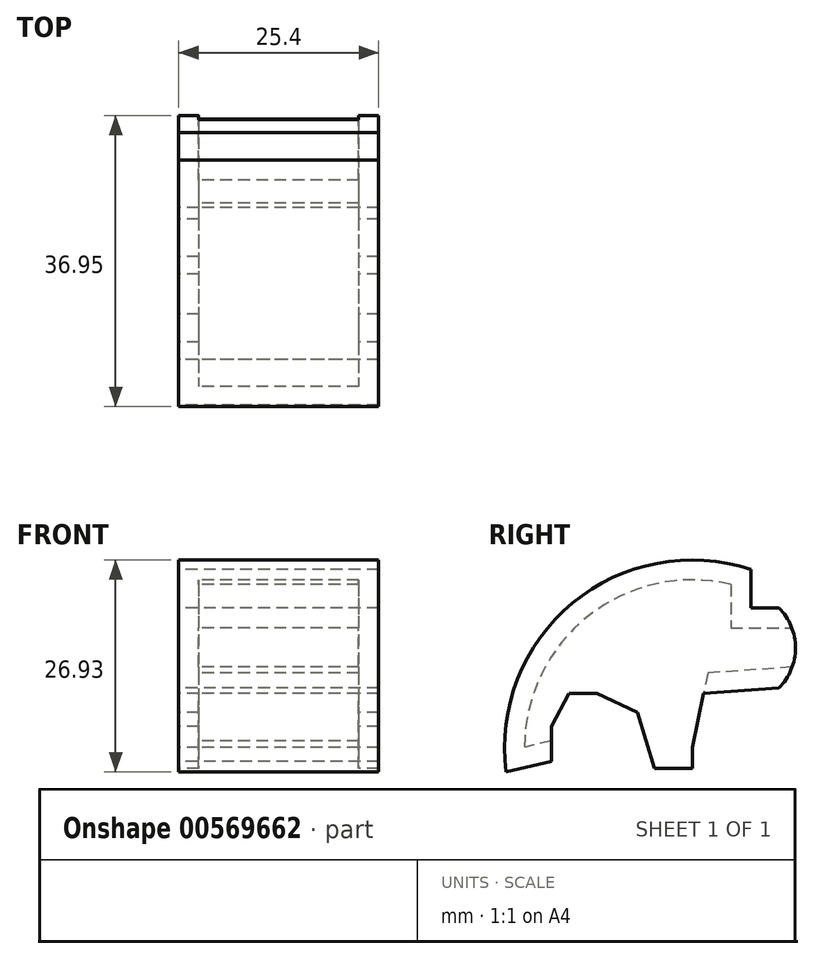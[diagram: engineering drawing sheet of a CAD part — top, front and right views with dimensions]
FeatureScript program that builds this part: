
annotation { "Feature Type Name" : "Feature", "Feature Type Description" : "" }
export const myFeature = defineFeature(function(context is Context, id is Id, definition is map)
    precondition{}
    {
        {
            var Q0;
            Q0=qCreatedBy(makeId("Right.planeOp"),FACE);
            var sketch = newSketch(context, id + "F0", { "sketchPlane" : qUnion([Q0])});
            skArc(sketch, "E0", {"start": v(39.95, 40) * mm, "mid": v(17.3, 35.7) * mm, "end": v(8.88, 14.25) * mm});
            skLineSegment(sketch, "E1", {"start": v(27.74, 14.7) * mm, "end": v(25.52, 21.8) * mm});
            skLineSegment(sketch, "E2", {"start": v(25.52, 21.8) * mm, "end": v(20.42, 24.24) * mm});
            skLineSegment(sketch, "E3", {"start": v(20.42, 24.24) * mm, "end": v(16.87, 24.24) * mm});
            skLineSegment(sketch, "E4", {"start": v(16.87, 24.24) * mm, "end": v(14.65, 20.02) * mm});
            skLineSegment(sketch, "E5", {"start": v(14.65, 20.02) * mm, "end": v(14.65, 15.58) * mm});
            skLineSegment(sketch, "E6", {"start": v(14.65, 15.58) * mm, "end": v(8.88, 14.25) * mm});
            skLineSegment(sketch, "E7", {"start": v(39.95, 40) * mm, "end": v(39.95, 35.1) * mm});
            skLineSegment(sketch, "E8", {"start": v(39.95, 35.1) * mm, "end": v(43.5, 35.1) * mm});
            skArc(sketch, "E9", {"start": v(43.5, 24.9) * mm, "mid": v(45.63, 30) * mm, "end": v(43.5, 35.1) * mm});
            skLineSegment(sketch, "E10", {"start": v(43.5, 24.9) * mm, "end": v(33.96, 24.24) * mm});
            skLineSegment(sketch, "E11", {"start": v(33.96, 24.24) * mm, "end": v(32.52, 17.34) * mm});
            skLineSegment(sketch, "E12", {"start": v(32.52, 14.7) * mm, "end": v(27.74, 14.7) * mm});
            skLineSegment(sketch, "E13", {"start": v(32.52, 17.34) * mm, "end": v(32.52, 14.7) * mm});
            skSolve(sketch);
        }
        {
            var Q0;
            Q0=makeQuery(id+"F0.imprint","IMPRINT",FACE,{"disambiguationData":[TD([[makeQuery(id+"F0.imprint","IMPRINT",EDGE,{"derivedFrom":sQuery(id+"F0.wireOp",EDGE,"E0")}),1.0]])]});
            extrude(context, id + "F1", {"entities" : qUnion([Q0]), "depth" : 25.4 * mm, "offsetDistance" : 25.4 * mm});
        }
        {
            var Q0;
            Q0=makeQuery(id+"F1.opExtrude","SWEPT_FACE",FACE,{"disambiguationData":[OSD([sQuery(id+"F0.wireOp",EDGE,"E5")])]});
            var Q1;
            Q1=makeQuery(id+"F1.opExtrude","SWEPT_FACE",FACE,{"disambiguationData":[OSD([sQuery(id+"F0.wireOp",EDGE,"E4")])]});
            var Q2;
            Q2=makeQuery(id+"F1.opExtrude","SWEPT_FACE",FACE,{"disambiguationData":[OSD([sQuery(id+"F0.wireOp",EDGE,"E11")])]});
            var Q3;
            Q3=makeQuery(id+"F1.opExtrude","SWEPT_FACE",FACE,{"disambiguationData":[OSD([sQuery(id+"F0.wireOp",EDGE,"E9")])]});
            var Q4;
            Q4=makeQuery(id+"F1.opExtrude","SWEPT_FACE",FACE,{"disambiguationData":[OSD([sQuery(id+"F0.wireOp",EDGE,"E12")])]});
            var Q5;
            Q5=makeQuery(id+"F1.opExtrude","SWEPT_FACE",FACE,{"disambiguationData":[OSD([sQuery(id+"F0.wireOp",EDGE,"E1")])]});
            var Q6;
            Q6=makeQuery(id+"F1.opExtrude","SWEPT_FACE",FACE,{"disambiguationData":[OSD([sQuery(id+"F0.wireOp",EDGE,"E2")])]});
            var Q7;
            Q7=makeQuery(id+"F1.opExtrude","SWEPT_FACE",FACE,{"disambiguationData":[OSD([sQuery(id+"F0.wireOp",EDGE,"E3")])]});
            shell(context, id + "F2", {"entities" : qUnion([Q0, Q1, Q2, Q3, Q4, Q5, Q6, Q7]), "thickness" : 2.54 * mm});
        }
        {
            var Q0;
            Q0=makeQuery(id+"F1.opExtrude","SWEPT_FACE",FACE,{"disambiguationData":[OSD([sQuery(id+"F0.wireOp",EDGE,"E13")])]});
            var sketch = newSketch(context, id + "F3", { "sketchPlane" : qUnion([Q0])});
            skLineSegment(sketch, "E14", {"start": v(-22.86, 17.34) * mm, "end": v(-22.86, 14.7) * mm});
            skLineSegment(sketch, "E15", {"start": v(-2.54, 17.34) * mm, "end": v(-2.54, 14.7) * mm});
            skLineSegment(sketch, "E16", {"start": v(-2.54, 14.7) * mm, "end": v(-22.86, 14.7) * mm});
            skLineSegment(sketch, "E17", {"start": v(-22.86, 17.34) * mm, "end": v(-2.54, 17.34) * mm});
            skSolve(sketch);
        }
        {
            var Q0;
            Q0=makeQuery(id+"F3.imprint","IMPRINT",FACE,{"disambiguationData":[TD([[makeQuery(id+"F3.imprint","IMPRINT",EDGE,{"derivedFrom":sQuery(id+"F3.wireOp",EDGE,"E14")}),1.0]])]});
            extrude(context, id + "F4", {"entities" : qUnion([Q0]), "operationType" : NewBodyOperationType.REMOVE, "oppositeDirection" : true, "depth" : 3.17 * mm, "offsetDistance" : 25.4 * mm});
        }
    });
